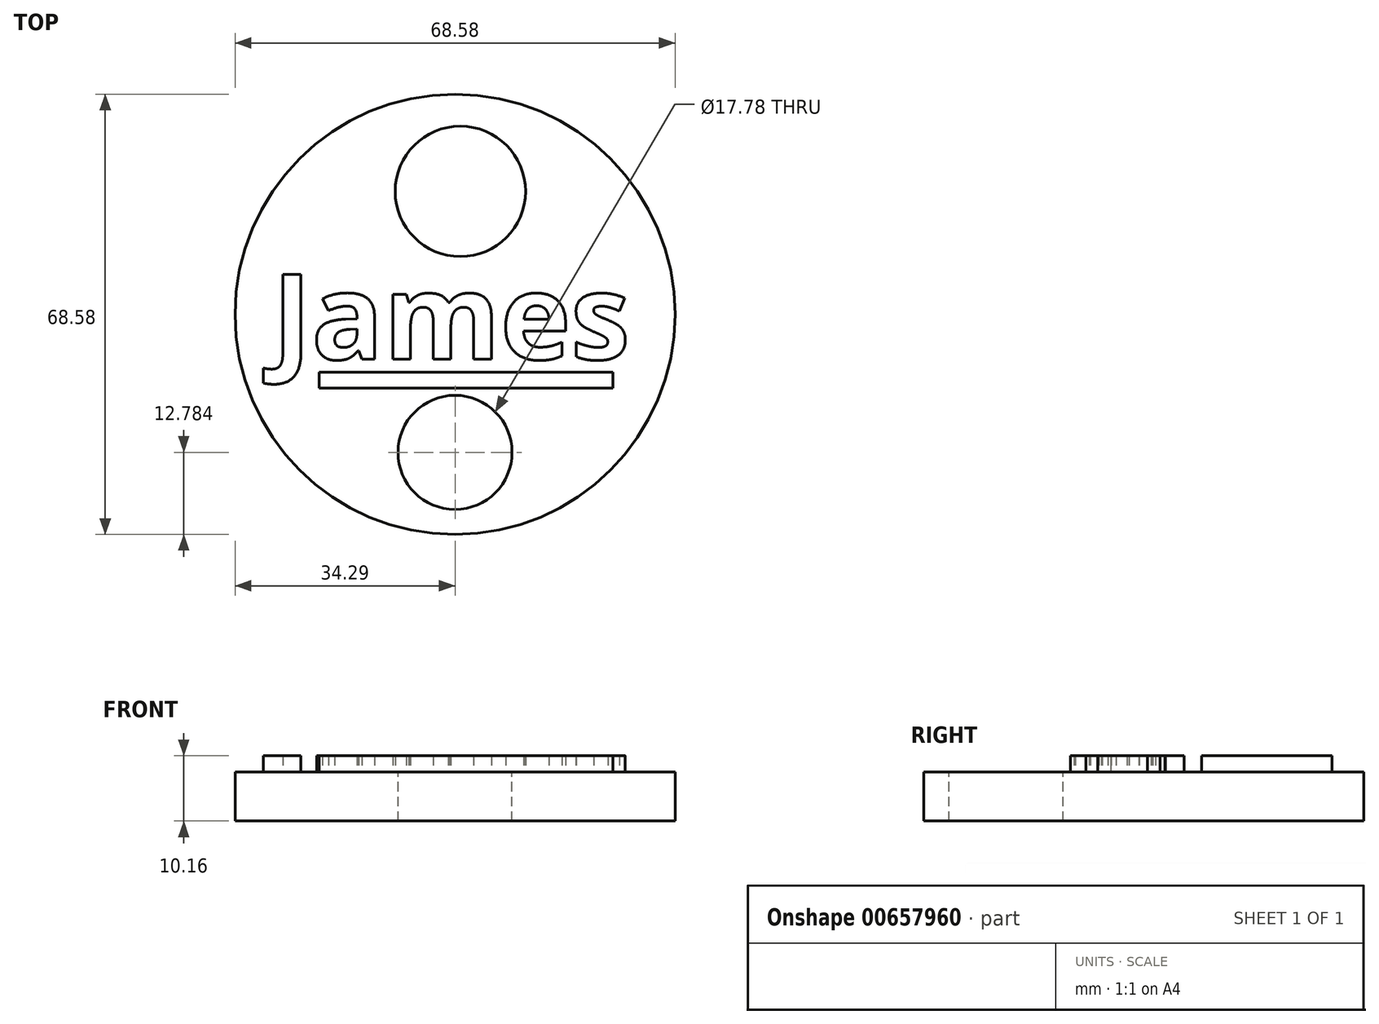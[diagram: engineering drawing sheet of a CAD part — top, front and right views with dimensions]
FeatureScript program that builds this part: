
annotation { "Feature Type Name" : "Feature", "Feature Type Description" : "" }
export const myFeature = defineFeature(function(context is Context, id is Id, definition is map)
    precondition{}
    {
        {
            var Q0;
            Q0=qCreatedBy(makeId("Top.planeOp"),FACE);
            var sketch = newSketch(context, id + "F0", { "sketchPlane" : qUnion([Q0])});
            skCircle(sketch, "E0", {"center": v(0, 0) * mm, "radius": 34.3 * mm});
            skSolve(sketch);
        }
        {
            var Q0;
            Q0=makeQuery(id+"F0.imprint","IMPRINT",FACE,{"disambiguationData":[TD([[makeQuery(id+"F0.imprint","IMPRINT",EDGE,{"derivedFrom":sQuery(id+"F0.wireOp",EDGE,"E0")}),1.0]])]});
            extrude(context, id + "F1", {"entities" : qUnion([Q0]), "depth" : 7.62 * mm, "offsetDistance" : 25.4 * mm});
        }
        {
            var Q0;
            Q0=makeQuery(id+"F1.opExtrude","CAP_FACE",FACE,{"disambiguationData":[OSD([sQuery(id+"F0.wireOp",EDGE,"E0")])],"isStart":true});
            var sketch = newSketch(context, id + "F2", { "sketchPlane" : qUnion([Q0])});
            skArc(sketch, "E1", {"start": v(-12.87, -31.78) * mm, "mid": v(-0.32, -60.7) * mm, "end": v(12.53, -31.92) * mm});
            skSolve(sketch);
        }
        {
            var Q0;
            {var subQ0=sQuery(id+"F2.wireOp",EDGE,"E1");Q0=makeQuery(id+"F2.imprint","IMPRINT",FACE,{"disambiguationData":[TD([[makeQuery(id+"F2.imprint","IMPRINT",EDGE,{"derivedFrom":subQ0}),1.0]])]});}
            extrude(context, id + "F3", {"entities" : qUnion([Q0]), "oppositeDirection" : true, "depth" : 7.62 * mm, "offsetDistance" : 25.4 * mm});
        }
        {
            var Q0;
            Q0=makeQuery(id+"F1.opExtrude","CAP_FACE",FACE,{"disambiguationData":[OSD([sQuery(id+"F0.wireOp",EDGE,"E0")])],"isStart":false});
            var sketch = newSketch(context, id + "F4", { "sketchPlane" : qUnion([Q0])});
            skText(sketch, "E2", { "text": "James", "fontName": "OpenSans-Bold.ttf"});
            const initialGuessF4  = {"E2": [-0.02851, -0.007, 1, 0, 0.01336]};
            skSetInitialGuess(sketch, initialGuessF4);
            skSolve(sketch);
        }
        {
            var Q0;
            Q0 = qSketchRegion(id + "F4", true);
            extrude(context, id + "F5", {"entities" : qUnion([Q0]), "operationType" : NewBodyOperationType.ADD, "depth" : 2.54 * mm, "offsetDistance" : 25.4 * mm});
        }
        {
            var Q0;
            {var subQ0=sQuery(id+"F0.wireOp",EDGE,"E0");Q0=makeQuery(id+"F5.boolean.opBoolean","SPLIT",FACE,{"disambiguationData":[TD([makeQuery(id+"F1.opExtrude","SWEPT_FACE",FACE,{"disambiguationData":[OSD([subQ0])]})])],"derivedFrom":makeQuery(id+"F1.opExtrude","CAP_FACE",FACE,{"disambiguationData":[OSD([subQ0])],"isStart":false})});}
            var sketch = newSketch(context, id + "F6", { "sketchPlane" : qUnion([Q0])});
            skCircle(sketch, "E3", {"center": v(0.84, 19.16) * mm, "radius": 10.16 * mm});
            skSolve(sketch);
        }
        {
            var Q0;
            Q0=makeQuery(id+"F6.imprint","IMPRINT",FACE,{"disambiguationData":[TD([[makeQuery(id+"F6.imprint","IMPRINT",EDGE,{"derivedFrom":sQuery(id+"F6.wireOp",EDGE,"E3")}),1.0]])]});
            var Q1;
            Q1=sQuery(id+"F6.wireOp",EDGE,"E3");
            extrude(context, id + "F7", {"entities" : qUnion([Q0]), "operationType" : NewBodyOperationType.ADD, "surfaceEntities" : qUnion([Q1]), "depth" : 2.54 * mm, "offsetDistance" : 25.4 * mm});
        }
        {
            var Q0;
            Q0=makeQuery(id+"F7.opExtrude","CAP_FACE",FACE,{"disambiguationData":[OSD([sQuery(id+"F6.wireOp",EDGE,"E3")])],"isStart":false});
            var sketch = newSketch(context, id + "F8", { "sketchPlane" : qUnion([Q0])});
            skArc(sketch, "E4", {"start": v(-4.45, 10.08) * mm, "mid": v(-2.57, 18.8) * mm, "end": v(-5.2, 27.34) * mm});
            skSolve(sketch);
        }
        {
            var Q0;
            Q0=makeQuery(id+"F3.opExtrude","CAP_FACE",FACE,{"disambiguationData":[OSD([sQuery(id+"F0.wireOp",EDGE,"E0"),sQuery(id+"F2.wireOp",EDGE,"E1")])],"isStart":false});
            var sketch = newSketch(context, id + "F9", { "sketchPlane" : qUnion([Q0])});
            skCircle(sketch, "E5", {"center": v(0, 49.18) * mm, "radius": 6.54 * mm});
            skSolve(sketch);
        }
        {
            var Q0;
            Q0=sQuery(id+"F9.wireOp",VERTEX,"E5.center");
            var Q1;
            Q1=makeQuery(id+"F3.opExtrude","SWEPT_BODY",BODY,{"disambiguationData":[OSD([sQuery(id+"F0.wireOp",EDGE,"E0"),sQuery(id+"F2.wireOp",EDGE,"E1")])]});
            hole(context, id + "F10", {"style" : HoleStyle.SIMPLE, "endStyle" : HoleEndStyle.THROUGH, "holeDiameter" : 15.24 * mm, "majorDiameter" : 6.35 * mm, "isTappedThrough" : true, "tappedDepth" : 12.7 * mm, "tapClearance" : 3, "locations" : qUnion([Q0]), "scope" : qUnion([Q1])});
        }
        {
            var Q0;
            {var subQ0=sQuery(id+"F0.wireOp",EDGE,"E0");Q0=makeQuery(id+"F5.boolean.opBoolean","SPLIT",FACE,{"disambiguationData":[TD([makeQuery(id+"F1.opExtrude","SWEPT_FACE",FACE,{"disambiguationData":[OSD([subQ0])]})])],"derivedFrom":makeQuery(id+"F1.opExtrude","CAP_FACE",FACE,{"disambiguationData":[OSD([subQ0])],"isStart":false})});}
            var sketch = newSketch(context, id + "F11", { "sketchPlane" : qUnion([Q0])});
            skLineSegment(sketch, "E6.bottom", {"start": v(-21.18, -11.46) * mm, "end": v(24.64, -11.46) * mm});
            skLineSegment(sketch, "E6.top", {"start": v(-21.18, -9.04) * mm, "end": v(24.64, -9.04) * mm});
            skLineSegment(sketch, "E6.left", {"start": v(-21.18, -11.46) * mm, "end": v(-21.18, -9.04) * mm});
            skLineSegment(sketch, "E6.right", {"start": v(24.64, -11.46) * mm, "end": v(24.64, -9.04) * mm});
            skSolve(sketch);
        }
        {
            var Q0;
            Q0=makeQuery(id+"F11.imprint","IMPRINT",FACE,{"disambiguationData":[TD([[makeQuery(id+"F11.imprint","IMPRINT",EDGE,{"derivedFrom":sQuery(id+"F11.wireOp",EDGE,"E6.bottom")}),1.0]])]});
            extrude(context, id + "F12", {"entities" : qUnion([Q0]), "operationType" : NewBodyOperationType.ADD, "depth" : 2.54 * mm, "offsetDistance" : 25.4 * mm});
        }
        {
            var Q0;
            Q0=makeQuery(id+"F3.opExtrude","SWEPT_BODY",BODY,{"disambiguationData":[OSD([sQuery(id+"F0.wireOp",EDGE,"E0"),sQuery(id+"F2.wireOp",EDGE,"E1")])]});
            deleteBodies(context, id + "F13", {"entities" : qUnion([Q0])});
        }
        {
            var Q0;
            {var subQ0=sQuery(id+"F0.wireOp",EDGE,"E0");Q0=makeQuery(id+"F5.boolean.opBoolean","SPLIT",FACE,{"disambiguationData":[TD([makeQuery(id+"F1.opExtrude","SWEPT_FACE",FACE,{"disambiguationData":[OSD([subQ0])]})])],"derivedFrom":makeQuery(id+"F1.opExtrude","CAP_FACE",FACE,{"disambiguationData":[OSD([subQ0])],"isStart":false})});}
            var sketch = newSketch(context, id + "F14", { "sketchPlane" : qUnion([Q0])});
            skCircle(sketch, "E7", {"center": v(0, -21.5) * mm, "radius": 7.38 * mm});
            skSolve(sketch);
        }
        {
            var Q0;
            Q0=sQuery(id+"F14.wireOp",VERTEX,"E7.center");
            var Q1;
            Q1=makeQuery(id+"F1.opExtrude","SWEPT_BODY",BODY,{"disambiguationData":[OSD([sQuery(id+"F0.wireOp",EDGE,"E0")])]});
            hole(context, id + "F15", {"style" : HoleStyle.SIMPLE, "endStyle" : HoleEndStyle.THROUGH, "holeDiameter" : 17.78 * mm, "majorDiameter" : 6.35 * mm, "isTappedThrough" : true, "tappedDepth" : 12.7 * mm, "tapClearance" : 3, "locations" : qUnion([Q0]), "scope" : qUnion([Q1])});
        }
    });
